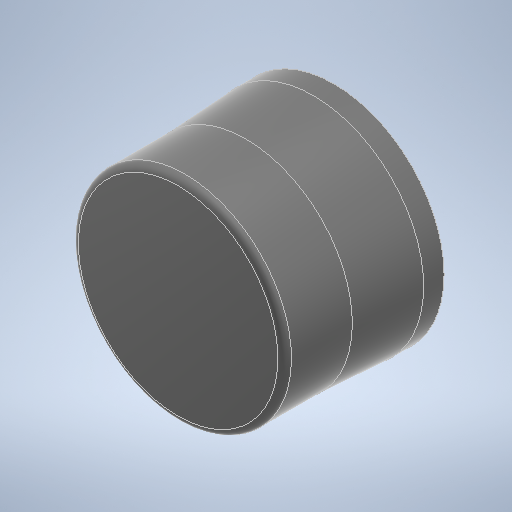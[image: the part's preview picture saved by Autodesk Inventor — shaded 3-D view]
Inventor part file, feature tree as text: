
AUTODESK INVENTOR PART (.ipt)
format: ipt  version: 2025.1 (Build 291241020, 241B)  size: 617,472 bytes
history: native  units: mm
features: revolve x2, sketch x2, fillet x1, projected_geometry x1
ambient origin geometry x8: Origin, YZ Plane, XZ Plane, XY Plane, X Axis, Y Axis, Z Axis, Center Point
bodies: Solid1 (feature_tree)
feature tree (6):
  revolve  "Revolution1"  [1 undecoded]
  revolve  "Revolution2"  [1 undecoded]
  fillet  "Fillet2"  [1 undecoded]
  sketch  "Sketch1"  dims[d0=15.75mm d1=10.2mm]
  sketch  "Sketch3"  dims[d2=10.0mm d3=5.0mm d4=360.0deg d14=0.8mm d15=16.3mm d16=10.0mm d17=90.0deg d18=3.0mm d19=0.8mm d20=1.0mm]
  projected_geometry  "Projected Loop1"
note: 3 required parameter values undecoded (feature->parameter linkage not recoverable at this tier; creation-order binding heuristic only, values carry confidence <= 0.55)